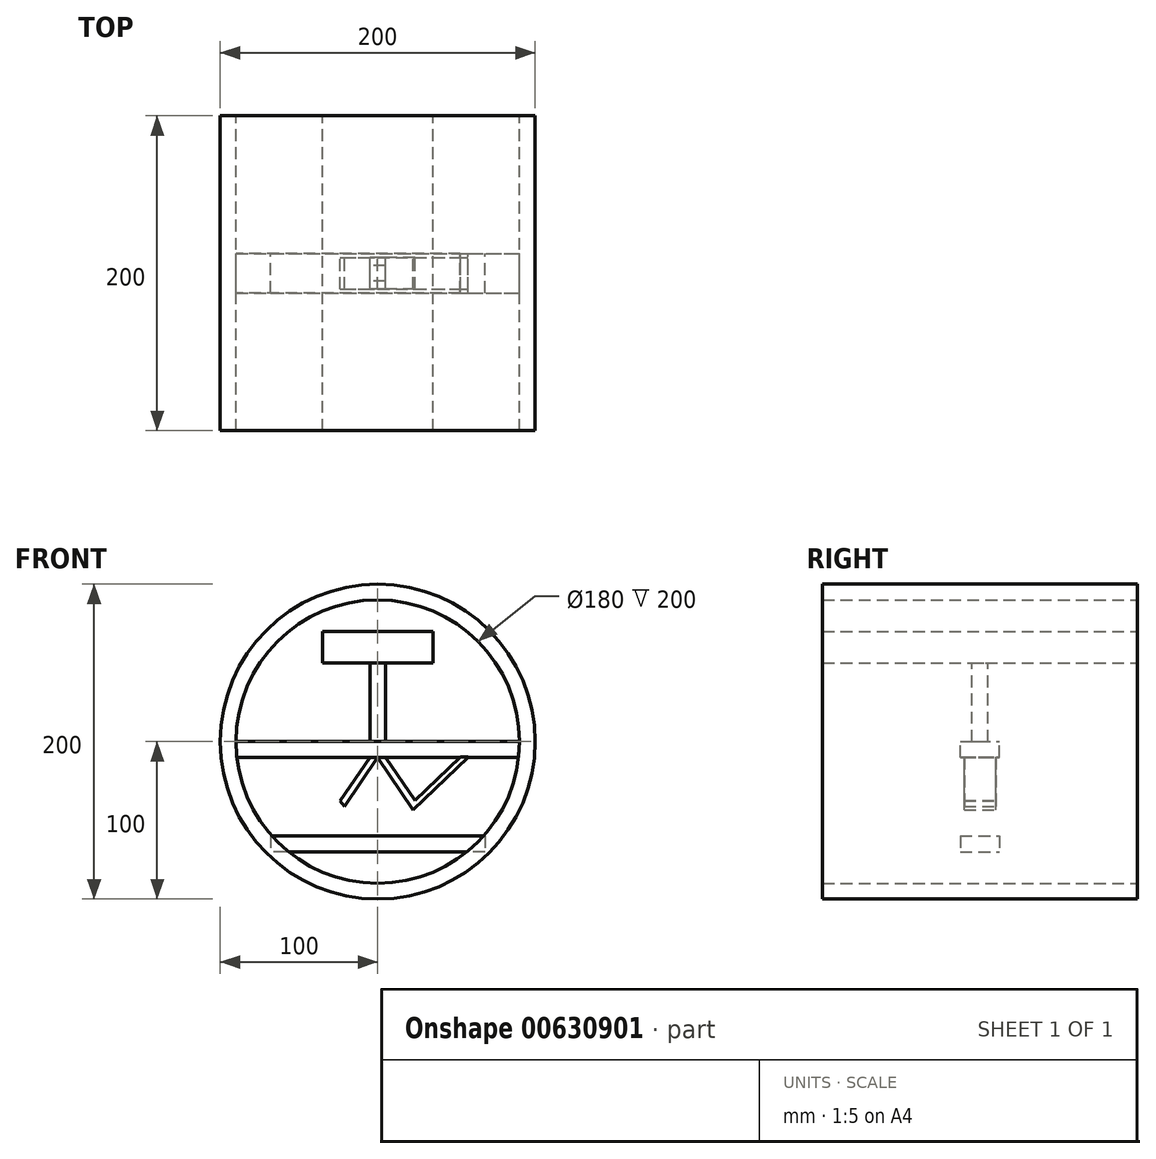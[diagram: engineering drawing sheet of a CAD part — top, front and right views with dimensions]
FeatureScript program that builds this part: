
annotation { "Feature Type Name" : "Feature", "Feature Type Description" : "" }
export const myFeature = defineFeature(function(context is Context, id is Id, definition is map)
    precondition{}
    {
        {
            var Q0;
            Q0=qCreatedBy(makeId("Front.planeOp"),FACE);
            var sketch = newSketch(context, id + "F0", { "sketchPlane" : qUnion([Q0])});
            skCircle(sketch, "E0", {"center": v(0, 0) * mm, "radius": 100 * mm});
            skLineSegment(sketch, "E1", {"start": v(0, 0) * mm, "end": v(100, 0) * mm});
            skSolve(sketch);
        }
        {
            var Q0;
            Q0 = qSketchRegion(id + "F0", true);
            extrude(context, id + "F1", {"entities" : qUnion([Q0]), "endBound" : BoundingType.SYMMETRIC, "depth" : 200 * mm, "offsetDistance" : 25 * mm});
        }
        {
            var Q0;
            Q0=makeQuery(id+"F1.opExtrude","CAP_FACE",FACE,{"disambiguationData":[OSD([sQuery(id+"F0.wireOp",EDGE,"E0")])],"isStart":true});
            var sketch = newSketch(context, id + "F2", { "sketchPlane" : qUnion([Q0])});
            skCircle(sketch, "E2", {"center": v(0, 0) * mm, "radius": 90 * mm});
            skLineSegment(sketch, "E3", {"start": v(0, 0) * mm, "end": v(90, 0) * mm});
            skSolve(sketch);
        }
        {
            var Q0;
            Q0 = qSketchRegion(id + "F2", true);
            extrude(context, id + "F3", {"entities" : qUnion([Q0]), "operationType" : NewBodyOperationType.REMOVE, "oppositeDirection" : true, "depth" : 200 * mm, "offsetDistance" : 25 * mm});
        }
        {
            var Q0;
            Q0=qCreatedBy(makeId("Front.planeOp"),FACE);
            var sketch = newSketch(context, id + "F4", { "sketchPlane" : qUnion([Q0])});
            skLineSegment(sketch, "E4", {"start": v(0, 0) * mm, "end": v(0, 60) * mm});
            skLineSegment(sketch, "E5.bottom", {"start": v(35, 50) * mm, "end": v(-35, 50) * mm});
            skLineSegment(sketch, "E5.top", {"start": v(35, 70) * mm, "end": v(-35, 70) * mm});
            skLineSegment(sketch, "E5.left", {"start": v(35, 50) * mm, "end": v(35, 70) * mm});
            skLineSegment(sketch, "E5.right", {"start": v(-35, 50) * mm, "end": v(-35, 70) * mm});
            skPoint(sketch, "E5.middle", {"position": v(0, 60) * mm});
            skLineSegment(sketch, "E6", {"start": v(0, 0) * mm, "end": v(-90, 0) * mm});
            skLineSegment(sketch, "E7", {"start": v(0, 0) * mm, "end": v(90, 0) * mm});
            skLineSegment(sketch, "E8.0", {"start": v(5, -10) * mm, "end": v(-90, -10) * mm});
            skLineSegment(sketch, "E9.0", {"start": v(5, 0) * mm, "end": v(5, 60) * mm});
            skLineSegment(sketch, "E10.0", {"start": v(-5, 0) * mm, "end": v(-5, 60) * mm});
            skLineSegment(sketch, "E11", {"start": v(-35, 50) * mm, "end": v(0, 50) * mm});
            skLineSegment(sketch, "E12", {"start": v(0, 50) * mm, "end": v(35, 50) * mm});
            skLineSegment(sketch, "E13", {"start": v(0, 0) * mm, "end": v(45, 0) * mm});
            skLineSegment(sketch, "E14", {"start": v(0, -60) * mm, "end": v(68, -60) * mm});
            skLineSegment(sketch, "E15", {"start": v(0, -60) * mm, "end": v(-68, -60) * mm});
            skLineSegment(sketch, "E16.0", {"start": v(0, -70) * mm, "end": v(-68, -70) * mm});
            skLineSegment(sketch, "E17", {"start": v(-90, -10) * mm, "end": v(-90, 0) * mm});
            skLineSegment(sketch, "E18", {"start": v(-68, -60) * mm, "end": v(-68, -70) * mm});
            skLineSegment(sketch, "E19", {"start": v(-42.5, -10) * mm, "end": v(-40.6, -10) * mm});
            skLineSegment(sketch, "E20", {"start": v(5, -10) * mm, "end": v(5, -10) * mm});
            skLineSegment(sketch, "E21", {"start": v(-68, -60) * mm, "end": v(-64.52, -60) * mm});
            skLineSegment(sketch, "E22", {"start": v(0, -60) * mm, "end": v(5, -60) * mm});
            skLineSegment(sketch, "E23", {"start": v(-34, -60) * mm, "end": v(0, -10) * mm});
            skLineSegment(sketch, "E24", {"start": v(0, -10) * mm, "end": v(34, -60) * mm});
            skLineSegment(sketch, "E25", {"start": v(-34, -60) * mm, "end": v(-39, -60) * mm});
            skLineSegment(sketch, "E26", {"start": v(-39, -60) * mm, "end": v(-5, -10) * mm});
            skLineSegment(sketch, "E27", {"start": v(34, -60) * mm, "end": v(39, -60) * mm});
            skLineSegment(sketch, "E28", {"start": v(39, -60) * mm, "end": v(5, -10) * mm});
            skLineSegment(sketch, "E29", {"start": v(-42.5, -10) * mm, "end": v(0, -60) * mm});
            skLineSegment(sketch, "E30", {"start": v(0, -60) * mm, "end": v(52.5, -9.86) * mm});
            skLineSegment(sketch, "E31", {"start": v(-42.5, -10) * mm, "end": v(-47.5, -10) * mm});
            skLineSegment(sketch, "E32", {"start": v(52.5, -9.86) * mm, "end": v(57.5, -9.85) * mm});
            skLineSegment(sketch, "E33", {"start": v(0, -60) * mm, "end": v(-5, -60) * mm});
            skLineSegment(sketch, "E34", {"start": v(-47.5, -10) * mm, "end": v(-5, -60) * mm});
            skLineSegment(sketch, "E35", {"start": v(5, -60) * mm, "end": v(57.5, -9.85) * mm});
            skLineSegment(sketch, "E36.0", {"start": v(0, -10) * mm, "end": v(90, -10) * mm});
            skLineSegment(sketch, "E37", {"start": v(90, 0) * mm, "end": v(90, -10) * mm});
            skLineSegment(sketch, "E38.0", {"start": v(0, -70) * mm, "end": v(68, -70) * mm});
            skLineSegment(sketch, "E39", {"start": v(68, -60) * mm, "end": v(68, -70) * mm});
            skSolve(sketch);
        }
        {
            var Q0;
            Q0=makeQuery(id+"F4.imprint","IMPRINT",FACE,{"disambiguationData":[TD([[makeQuery(id+"F4.imprint","IMPRINT",EDGE,{"derivedFrom":sQuery(id+"F4.wireOp",EDGE,"E5.top")}),1.0]])]});
            extrude(context, id + "F5", {"entities" : qUnion([Q0]), "endBound" : BoundingType.SYMMETRIC, "depth" : 200 * mm, "offsetDistance" : 25 * mm});
        }
        {
            var Q0;
            {var subQ0=sQuery(id+"F4.wireOp",EDGE,"E6");var subQ5=sQuery(id+"F4.wireOp",EDGE,"E10.0");var subQ6=makeQuery(id+"F4.imprint","INTERSECT",VERTEX,{"derivedFrom":[subQ0,subQ5]});Q0=makeQuery(id+"F4.imprint","IMPRINT",FACE,{"disambiguationData":[TD([[makeQuery(id+"F4.imprint","IMPRINT",EDGE,{"disambiguationData":[TD([[subQ6,-1.0]])],"derivedFrom":subQ5}),-1.0]])]});}
            var Q1;
            {var subQ0=sQuery(id+"F4.wireOp",EDGE,"E13");var subQ5=sQuery(id+"F4.wireOp",EDGE,"E9.0");var subQ6=makeQuery(id+"F4.imprint","INTERSECT",VERTEX,{"derivedFrom":[subQ5,subQ0]});Q1=makeQuery(id+"F4.imprint","IMPRINT",FACE,{"disambiguationData":[TD([[makeQuery(id+"F4.imprint","IMPRINT",EDGE,{"disambiguationData":[TD([[subQ6,-1.0]])],"derivedFrom":subQ5}),1.0]])]});}
            extrude(context, id + "F6", {"entities" : qUnion([Q0, Q1]), "operationType" : NewBodyOperationType.ADD, "endBound" : BoundingType.SYMMETRIC, "depth" : 10 * mm, "offsetDistance" : 25 * mm});
        }
        {
            var Q0;
            {var subQ14=sQuery(id+"F4.wireOp",EDGE,"E7");Q0=makeQuery(id+"F4.imprint","IMPRINT",FACE,{"disambiguationData":[TD([[makeQuery(id+"F4.imprint","IMPRINT",EDGE,{"derivedFrom":subQ14}),-1.0]])]});}
            var Q1;
            {var subQ2=sQuery(id+"F4.wireOp",EDGE,"E16.0");Q1=makeQuery(id+"F4.imprint","IMPRINT",FACE,{"disambiguationData":[TD([[makeQuery(id+"F4.imprint","IMPRINT",EDGE,{"derivedFrom":subQ2}),-1.0]])]});}
            extrude(context, id + "F7", {"entities" : qUnion([Q0, Q1]), "endBound" : BoundingType.SYMMETRIC, "depth" : 25 * mm, "offsetDistance" : 25 * mm});
        }
        {
            var Q0;
            {var subQ5=sQuery(id+"F4.wireOp",EDGE,"E31");Q0=makeQuery(id+"F4.imprint","IMPRINT",FACE,{"disambiguationData":[TD([[makeQuery(id+"F4.imprint","IMPRINT",EDGE,{"derivedFrom":subQ5}),1.0]])]});}
            var Q1;
            {var subQ0=sQuery(id+"F4.wireOp",EDGE,"E25");Q1=makeQuery(id+"F4.imprint","IMPRINT",FACE,{"disambiguationData":[TD([[makeQuery(id+"F4.imprint","IMPRINT",EDGE,{"derivedFrom":subQ0}),-1.0]])]});}
            var Q2;
            {var subQ0=sQuery(id+"F4.wireOp",EDGE,"E34");var subQ1=sQuery(id+"F4.wireOp",EDGE,"E23");var subQ2=makeQuery(id+"F4.imprint","INTERSECT",VERTEX,{"derivedFrom":[subQ1,subQ0]});Q2=makeQuery(id+"F4.imprint","IMPRINT",FACE,{"disambiguationData":[TD([[makeQuery(id+"F4.imprint","IMPRINT",EDGE,{"disambiguationData":[TD([[subQ2,-1.0]])],"derivedFrom":subQ1}),1.0]])]});}
            var Q3;
            {var subQ1=sQuery(id+"F4.wireOp",EDGE,"E8.0");var subQ3=sQuery(id+"F4.wireOp",EDGE,"E26");var subQ4=makeQuery(id+"F4.imprint","INTERSECT",VERTEX,{"derivedFrom":[subQ1,subQ3]});Q3=makeQuery(id+"F4.imprint","IMPRINT",FACE,{"disambiguationData":[TD([[makeQuery(id+"F4.imprint","IMPRINT",EDGE,{"disambiguationData":[TD([[subQ4,1.0]])],"derivedFrom":subQ3}),-1.0]])]});}
            var Q4;
            {var subQ5=sQuery(id+"F4.wireOp",EDGE,"E33");Q4=makeQuery(id+"F4.imprint","IMPRINT",FACE,{"disambiguationData":[TD([[makeQuery(id+"F4.imprint","IMPRINT",EDGE,{"derivedFrom":subQ5}),-1.0]])]});}
            var Q5;
            {var subQ0=sQuery(id+"F4.wireOp",EDGE,"E22");Q5=makeQuery(id+"F4.imprint","IMPRINT",FACE,{"disambiguationData":[TD([[makeQuery(id+"F4.imprint","IMPRINT",EDGE,{"derivedFrom":subQ0}),1.0]])]});}
            var Q6;
            {var subQ0=sQuery(id+"F4.wireOp",EDGE,"E30");var subQ1=sQuery(id+"F4.wireOp",EDGE,"E24");var subQ2=makeQuery(id+"F4.imprint","INTERSECT",VERTEX,{"derivedFrom":[subQ1,subQ0]});Q6=makeQuery(id+"F4.imprint","IMPRINT",FACE,{"disambiguationData":[TD([[makeQuery(id+"F4.imprint","IMPRINT",EDGE,{"disambiguationData":[TD([[subQ2,-1.0]])],"derivedFrom":subQ1}),1.0]])]});}
            var Q7;
            {var subQ0=sQuery(id+"F4.wireOp",EDGE,"E20");Q7=makeQuery(id+"F4.imprint","IMPRINT",FACE,{"disambiguationData":[TD([[makeQuery(id+"F4.imprint","IMPRINT",EDGE,{"derivedFrom":subQ0}),-1.0]])]});}
            var Q8;
            {var subQ0=sQuery(id+"F4.wireOp",EDGE,"E27");Q8=makeQuery(id+"F4.imprint","IMPRINT",FACE,{"disambiguationData":[TD([[makeQuery(id+"F4.imprint","IMPRINT",EDGE,{"derivedFrom":subQ0}),1.0]])]});}
            var Q9;
            {var subQ5=sQuery(id+"F4.wireOp",EDGE,"E32");Q9=makeQuery(id+"F4.imprint","IMPRINT",FACE,{"disambiguationData":[TD([[makeQuery(id+"F4.imprint","IMPRINT",EDGE,{"derivedFrom":subQ5}),-1.0]])]});}
            var Q10;
            {var subQ0=sQuery(id+"F4.wireOp",EDGE,"E36.0");var subQ5=sQuery(id+"F4.wireOp",EDGE,"E28");var subQ6=makeQuery(id+"F4.imprint","INTERSECT",VERTEX,{"derivedFrom":[subQ5,subQ0]});Q10=makeQuery(id+"F4.imprint","IMPRINT",FACE,{"disambiguationData":[TD([[makeQuery(id+"F4.imprint","IMPRINT",EDGE,{"disambiguationData":[TD([[subQ6,1.0]])],"derivedFrom":subQ5}),1.0]])]});}
            var Q11;
            {var subQ0=sQuery(id+"F4.wireOp",EDGE,"E35");var subQ1=sQuery(id+"F4.wireOp",EDGE,"E28");var subQ2=makeQuery(id+"F4.imprint","INTERSECT",VERTEX,{"derivedFrom":[subQ1,subQ0]});Q11=makeQuery(id+"F4.imprint","IMPRINT",FACE,{"disambiguationData":[TD([[makeQuery(id+"F4.imprint","IMPRINT",EDGE,{"disambiguationData":[TD([[subQ2,-1.0]])],"derivedFrom":subQ1}),-1.0]])]});}
            extrude(context, id + "F8", {"entities" : qUnion([Q0, Q1, Q2, Q3, Q4, Q5, Q6, Q7, Q8, Q9, Q10, Q11]), "endBound" : BoundingType.SYMMETRIC, "depth" : 20 * mm, "offsetDistance" : 25 * mm});
        }
    });
